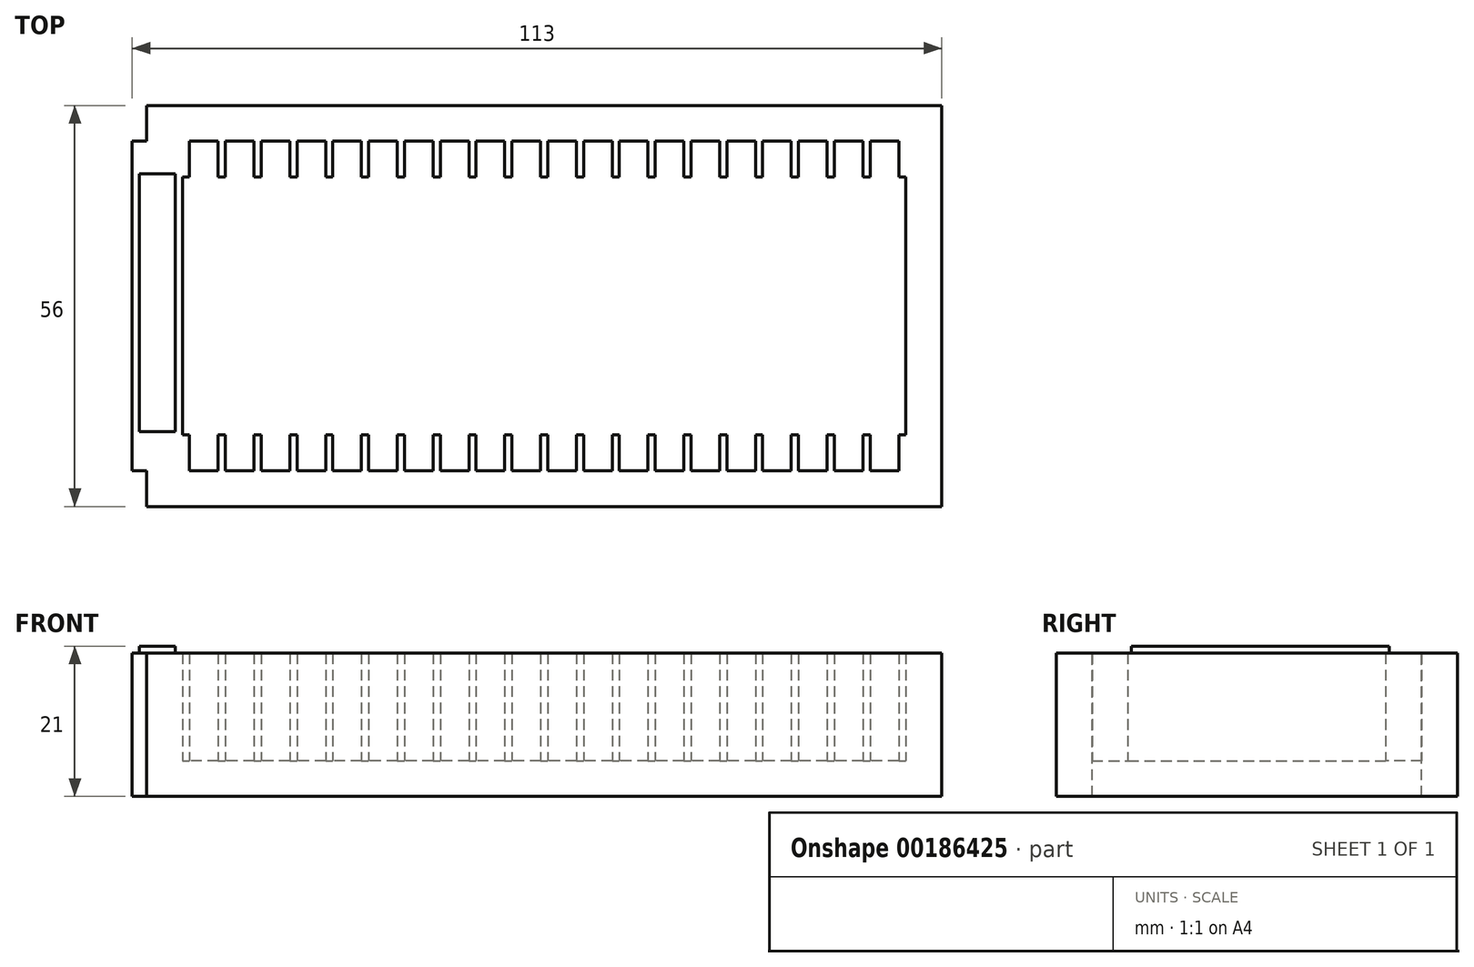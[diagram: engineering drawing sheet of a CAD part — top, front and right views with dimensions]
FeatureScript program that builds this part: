
annotation { "Feature Type Name" : "Feature", "Feature Type Description" : "" }
export const myFeature = defineFeature(function(context is Context, id is Id, definition is map)
    precondition{}
    {
        {
            var Q0;
            Q0=qCreatedBy(makeId("Top.planeOp"),FACE);
            var sketch = newSketch(context, id + "F0", { "sketchPlane" : qUnion([Q0])});
            skLineSegment(sketch, "E0.bottom", {"start": v(-50.5, 23) * mm, "end": v(50.5, 23) * mm});
            skLineSegment(sketch, "E0.top", {"start": v(-50.5, -23) * mm, "end": v(50.5, -23) * mm});
            skLineSegment(sketch, "E0.left", {"start": v(-50.5, 23) * mm, "end": v(-50.5, -23) * mm});
            skLineSegment(sketch, "E0.right", {"start": v(50.5, 23) * mm, "end": v(50.5, -23) * mm});
            skPoint(sketch, "E0.middle", {"position": v(0, 0) * mm});
            skSolve(sketch);
        }
        {
            var Q0;
            Q0=qCreatedBy(makeId("Top.planeOp"),FACE);
            var sketch = newSketch(context, id + "F1", { "sketchPlane" : qUnion([Q0])});
            skLineSegment(sketch, "E1.bottom", {"start": v(-50.5, 23) * mm, "end": v(-49.5, 23) * mm});
            skLineSegment(sketch, "E1.top", {"start": v(-50.5, 18) * mm, "end": v(-49.5, 18) * mm});
            skLineSegment(sketch, "E1.left", {"start": v(-50.5, 23) * mm, "end": v(-50.5, 18) * mm});
            skLineSegment(sketch, "E1.right", {"start": v(-49.5, 23) * mm, "end": v(-49.5, 18) * mm});
            skLineSegment(sketch, "E2.1.0.0", {"start": v(-45.5, 23) * mm, "end": v(-44.5, 23) * mm});
            skLineSegment(sketch, "E2.1.0.1", {"start": v(-45.5, 18) * mm, "end": v(-44.5, 18) * mm});
            skLineSegment(sketch, "E2.1.0.2", {"start": v(-45.5, 23) * mm, "end": v(-45.5, 18) * mm});
            skLineSegment(sketch, "E2.1.0.3", {"start": v(-44.5, 23) * mm, "end": v(-44.5, 18) * mm});
            skLineSegment(sketch, "E2.2.0.0", {"start": v(-40.5, 23) * mm, "end": v(-39.5, 23) * mm});
            skLineSegment(sketch, "E2.2.0.1", {"start": v(-40.5, 18) * mm, "end": v(-39.5, 18) * mm});
            skLineSegment(sketch, "E2.2.0.2", {"start": v(-40.5, 23) * mm, "end": v(-40.5, 18) * mm});
            skLineSegment(sketch, "E2.2.0.3", {"start": v(-39.5, 23) * mm, "end": v(-39.5, 18) * mm});
            skLineSegment(sketch, "E2.3.0.0", {"start": v(-35.5, 23) * mm, "end": v(-34.5, 23) * mm});
            skLineSegment(sketch, "E2.3.0.1", {"start": v(-35.5, 18) * mm, "end": v(-34.5, 18) * mm});
            skLineSegment(sketch, "E2.3.0.2", {"start": v(-35.5, 23) * mm, "end": v(-35.5, 18) * mm});
            skLineSegment(sketch, "E2.3.0.3", {"start": v(-34.5, 23) * mm, "end": v(-34.5, 18) * mm});
            skLineSegment(sketch, "E2.4.0.0", {"start": v(-30.5, 23) * mm, "end": v(-29.5, 23) * mm});
            skLineSegment(sketch, "E2.4.0.1", {"start": v(-30.5, 18) * mm, "end": v(-29.5, 18) * mm});
            skLineSegment(sketch, "E2.4.0.2", {"start": v(-30.5, 23) * mm, "end": v(-30.5, 18) * mm});
            skLineSegment(sketch, "E2.4.0.3", {"start": v(-29.5, 23) * mm, "end": v(-29.5, 18) * mm});
            skLineSegment(sketch, "E2.5.0.0", {"start": v(-25.5, 23) * mm, "end": v(-24.5, 23) * mm});
            skLineSegment(sketch, "E2.5.0.1", {"start": v(-25.5, 18) * mm, "end": v(-24.5, 18) * mm});
            skLineSegment(sketch, "E2.5.0.2", {"start": v(-25.5, 23) * mm, "end": v(-25.5, 18) * mm});
            skLineSegment(sketch, "E2.5.0.3", {"start": v(-24.5, 23) * mm, "end": v(-24.5, 18) * mm});
            skLineSegment(sketch, "E2.6.0.0", {"start": v(-20.5, 23) * mm, "end": v(-19.5, 23) * mm});
            skLineSegment(sketch, "E2.6.0.1", {"start": v(-20.5, 18) * mm, "end": v(-19.5, 18) * mm});
            skLineSegment(sketch, "E2.6.0.2", {"start": v(-20.5, 23) * mm, "end": v(-20.5, 18) * mm});
            skLineSegment(sketch, "E2.6.0.3", {"start": v(-19.5, 23) * mm, "end": v(-19.5, 18) * mm});
            skLineSegment(sketch, "E2.7.0.0", {"start": v(-15.5, 23) * mm, "end": v(-14.5, 23) * mm});
            skLineSegment(sketch, "E2.7.0.1", {"start": v(-15.5, 18) * mm, "end": v(-14.5, 18) * mm});
            skLineSegment(sketch, "E2.7.0.2", {"start": v(-15.5, 23) * mm, "end": v(-15.5, 18) * mm});
            skLineSegment(sketch, "E2.7.0.3", {"start": v(-14.5, 23) * mm, "end": v(-14.5, 18) * mm});
            skLineSegment(sketch, "E2.8.0.0", {"start": v(-10.5, 23) * mm, "end": v(-9.5, 23) * mm});
            skLineSegment(sketch, "E2.8.0.1", {"start": v(-10.5, 18) * mm, "end": v(-9.5, 18) * mm});
            skLineSegment(sketch, "E2.8.0.2", {"start": v(-10.5, 23) * mm, "end": v(-10.5, 18) * mm});
            skLineSegment(sketch, "E2.8.0.3", {"start": v(-9.5, 23) * mm, "end": v(-9.5, 18) * mm});
            skLineSegment(sketch, "E2.9.0.0", {"start": v(-5.5, 23) * mm, "end": v(-4.5, 23) * mm});
            skLineSegment(sketch, "E2.9.0.1", {"start": v(-5.5, 18) * mm, "end": v(-4.5, 18) * mm});
            skLineSegment(sketch, "E2.9.0.2", {"start": v(-5.5, 23) * mm, "end": v(-5.5, 18) * mm});
            skLineSegment(sketch, "E2.9.0.3", {"start": v(-4.5, 23) * mm, "end": v(-4.5, 18) * mm});
            skLineSegment(sketch, "E2.10.0.0", {"start": v(-0.5, 23) * mm, "end": v(0.5, 23) * mm});
            skLineSegment(sketch, "E2.10.0.1", {"start": v(-0.5, 18) * mm, "end": v(0.5, 18) * mm});
            skLineSegment(sketch, "E2.10.0.2", {"start": v(-0.5, 23) * mm, "end": v(-0.5, 18) * mm});
            skLineSegment(sketch, "E2.10.0.3", {"start": v(0.5, 23) * mm, "end": v(0.5, 18) * mm});
            skLineSegment(sketch, "E2.11.0.0", {"start": v(4.5, 23) * mm, "end": v(5.5, 23) * mm});
            skLineSegment(sketch, "E2.11.0.1", {"start": v(4.5, 18) * mm, "end": v(5.5, 18) * mm});
            skLineSegment(sketch, "E2.11.0.2", {"start": v(4.5, 23) * mm, "end": v(4.5, 18) * mm});
            skLineSegment(sketch, "E2.11.0.3", {"start": v(5.5, 23) * mm, "end": v(5.5, 18) * mm});
            skLineSegment(sketch, "E2.12.0.0", {"start": v(9.5, 23) * mm, "end": v(10.5, 23) * mm});
            skLineSegment(sketch, "E2.12.0.1", {"start": v(9.5, 18) * mm, "end": v(10.5, 18) * mm});
            skLineSegment(sketch, "E2.12.0.2", {"start": v(9.5, 23) * mm, "end": v(9.5, 18) * mm});
            skLineSegment(sketch, "E2.12.0.3", {"start": v(10.5, 23) * mm, "end": v(10.5, 18) * mm});
            skLineSegment(sketch, "E2.13.0.0", {"start": v(14.5, 23) * mm, "end": v(15.5, 23) * mm});
            skLineSegment(sketch, "E2.13.0.1", {"start": v(14.5, 18) * mm, "end": v(15.5, 18) * mm});
            skLineSegment(sketch, "E2.13.0.2", {"start": v(14.5, 23) * mm, "end": v(14.5, 18) * mm});
            skLineSegment(sketch, "E2.13.0.3", {"start": v(15.5, 23) * mm, "end": v(15.5, 18) * mm});
            skLineSegment(sketch, "E2.14.0.0", {"start": v(19.5, 23) * mm, "end": v(20.5, 23) * mm});
            skLineSegment(sketch, "E2.14.0.1", {"start": v(19.5, 18) * mm, "end": v(20.5, 18) * mm});
            skLineSegment(sketch, "E2.14.0.2", {"start": v(19.5, 23) * mm, "end": v(19.5, 18) * mm});
            skLineSegment(sketch, "E2.14.0.3", {"start": v(20.5, 23) * mm, "end": v(20.5, 18) * mm});
            skLineSegment(sketch, "E2.15.0.0", {"start": v(24.5, 23) * mm, "end": v(25.5, 23) * mm});
            skLineSegment(sketch, "E2.15.0.1", {"start": v(24.5, 18) * mm, "end": v(25.5, 18) * mm});
            skLineSegment(sketch, "E2.15.0.2", {"start": v(24.5, 23) * mm, "end": v(24.5, 18) * mm});
            skLineSegment(sketch, "E2.15.0.3", {"start": v(25.5, 23) * mm, "end": v(25.5, 18) * mm});
            skLineSegment(sketch, "E2.16.0.0", {"start": v(29.5, 23) * mm, "end": v(30.5, 23) * mm});
            skLineSegment(sketch, "E2.16.0.1", {"start": v(29.5, 18) * mm, "end": v(30.5, 18) * mm});
            skLineSegment(sketch, "E2.16.0.2", {"start": v(29.5, 23) * mm, "end": v(29.5, 18) * mm});
            skLineSegment(sketch, "E2.16.0.3", {"start": v(30.5, 23) * mm, "end": v(30.5, 18) * mm});
            skLineSegment(sketch, "E2.17.0.0", {"start": v(34.5, 23) * mm, "end": v(35.5, 23) * mm});
            skLineSegment(sketch, "E2.17.0.1", {"start": v(34.5, 18) * mm, "end": v(35.5, 18) * mm});
            skLineSegment(sketch, "E2.17.0.2", {"start": v(34.5, 23) * mm, "end": v(34.5, 18) * mm});
            skLineSegment(sketch, "E2.17.0.3", {"start": v(35.5, 23) * mm, "end": v(35.5, 18) * mm});
            skLineSegment(sketch, "E2.18.0.0", {"start": v(39.5, 23) * mm, "end": v(40.5, 23) * mm});
            skLineSegment(sketch, "E2.18.0.1", {"start": v(39.5, 18) * mm, "end": v(40.5, 18) * mm});
            skLineSegment(sketch, "E2.18.0.2", {"start": v(39.5, 23) * mm, "end": v(39.5, 18) * mm});
            skLineSegment(sketch, "E2.18.0.3", {"start": v(40.5, 23) * mm, "end": v(40.5, 18) * mm});
            skLineSegment(sketch, "E2.19.0.0", {"start": v(44.5, 23) * mm, "end": v(45.5, 23) * mm});
            skLineSegment(sketch, "E2.19.0.1", {"start": v(44.5, 18) * mm, "end": v(45.5, 18) * mm});
            skLineSegment(sketch, "E2.19.0.2", {"start": v(44.5, 23) * mm, "end": v(44.5, 18) * mm});
            skLineSegment(sketch, "E2.19.0.3", {"start": v(45.5, 23) * mm, "end": v(45.5, 18) * mm});
            skLineSegment(sketch, "E2.20.0.0", {"start": v(49.5, 23) * mm, "end": v(50.5, 23) * mm});
            skLineSegment(sketch, "E2.20.0.1", {"start": v(49.5, 18) * mm, "end": v(50.5, 18) * mm});
            skLineSegment(sketch, "E2.20.0.2", {"start": v(49.5, 23) * mm, "end": v(49.5, 18) * mm});
            skLineSegment(sketch, "E2.20.0.3", {"start": v(50.5, 23) * mm, "end": v(50.5, 18) * mm});
            skLineSegment(sketch, "E2.direction1", {"start": v(-50.5, 18) * mm, "end": v(-45.5, 18) * mm, "construction": true});
            skLineSegment(sketch, "E3.MirrorCS", {"start": v(-50.5, -23) * mm, "end": v(-49.5, -23) * mm});
            skLineSegment(sketch, "E4.MirrorCS", {"start": v(49.5, -23) * mm, "end": v(50.5, -23) * mm});
            skLineSegment(sketch, "E5.MirrorCS", {"start": v(-45.5, -18) * mm, "end": v(-44.5, -18) * mm});
            skLineSegment(sketch, "E6.MirrorCS", {"start": v(-50.5, -18) * mm, "end": v(-49.5, -18) * mm});
            skLineSegment(sketch, "E7.MirrorCS", {"start": v(-0.5, -18) * mm, "end": v(0.5, -18) * mm});
            skLineSegment(sketch, "E8.MirrorCS", {"start": v(19.5, -18) * mm, "end": v(20.5, -18) * mm});
            skLineSegment(sketch, "E9.MirrorCS", {"start": v(39.5, -18) * mm, "end": v(40.5, -18) * mm});
            skLineSegment(sketch, "E10.MirrorCS", {"start": v(-20.5, -18) * mm, "end": v(-19.5, -18) * mm});
            skLineSegment(sketch, "E11.MirrorCS", {"start": v(29.5, -18) * mm, "end": v(30.5, -18) * mm});
            skLineSegment(sketch, "E12.MirrorCS", {"start": v(49.5, -18) * mm, "end": v(50.5, -18) * mm});
            skLineSegment(sketch, "E13.MirrorCS", {"start": v(-35.5, -23) * mm, "end": v(-34.5, -23) * mm});
            skLineSegment(sketch, "E14.MirrorCS", {"start": v(-30.5, -18) * mm, "end": v(-29.5, -18) * mm});
            skLineSegment(sketch, "E15.MirrorCS", {"start": v(-10.5, -18) * mm, "end": v(-9.5, -18) * mm});
            skLineSegment(sketch, "E16.MirrorCS", {"start": v(9.5, -18) * mm, "end": v(10.5, -18) * mm});
            skLineSegment(sketch, "E17.MirrorCS", {"start": v(-40.5, -18) * mm, "end": v(-39.5, -18) * mm});
            skLineSegment(sketch, "E18.MirrorCS", {"start": v(-40.5, -23) * mm, "end": v(-39.5, -23) * mm});
            skLineSegment(sketch, "E19.MirrorCS", {"start": v(-0.5, -23) * mm, "end": v(0.5, -23) * mm});
            skLineSegment(sketch, "E20.MirrorCS", {"start": v(39.5, -23) * mm, "end": v(40.5, -23) * mm});
            skLineSegment(sketch, "E21.MirrorCS", {"start": v(19.5, -23) * mm, "end": v(20.5, -23) * mm});
            skLineSegment(sketch, "E22.MirrorCS", {"start": v(-45.5, -23) * mm, "end": v(-44.5, -23) * mm});
            skLineSegment(sketch, "E23.MirrorCS", {"start": v(-20.5, -23) * mm, "end": v(-19.5, -23) * mm});
            skLineSegment(sketch, "E24.MirrorCS", {"start": v(-35.5, -18) * mm, "end": v(-34.5, -18) * mm});
            skLineSegment(sketch, "E25.MirrorCS", {"start": v(-30.5, -23) * mm, "end": v(-29.5, -23) * mm});
            skLineSegment(sketch, "E26.MirrorCS", {"start": v(-10.5, -23) * mm, "end": v(-9.5, -23) * mm});
            skLineSegment(sketch, "E27.MirrorCS", {"start": v(9.5, -23) * mm, "end": v(10.5, -23) * mm});
            skLineSegment(sketch, "E28.MirrorCS", {"start": v(29.5, -23) * mm, "end": v(30.5, -23) * mm});
            skLineSegment(sketch, "E29.MirrorCS", {"start": v(34.5, -18) * mm, "end": v(35.5, -18) * mm});
            skLineSegment(sketch, "E30.MirrorCS", {"start": v(-25.5, -18) * mm, "end": v(-24.5, -18) * mm});
            skLineSegment(sketch, "E31.MirrorCS", {"start": v(-5.5, -18) * mm, "end": v(-4.5, -18) * mm});
            skLineSegment(sketch, "E32.MirrorCS", {"start": v(14.5, -18) * mm, "end": v(15.5, -18) * mm});
            skLineSegment(sketch, "E33.MirrorCS", {"start": v(4.5, -23) * mm, "end": v(5.5, -23) * mm});
            skLineSegment(sketch, "E34.MirrorCS", {"start": v(24.5, -23) * mm, "end": v(25.5, -23) * mm});
            skLineSegment(sketch, "E35.MirrorCS", {"start": v(44.5, -23) * mm, "end": v(45.5, -23) * mm});
            skLineSegment(sketch, "E36.MirrorCS", {"start": v(-15.5, -23) * mm, "end": v(-14.5, -23) * mm});
            skLineSegment(sketch, "E37.MirrorCS", {"start": v(24.5, -18) * mm, "end": v(25.5, -18) * mm});
            skLineSegment(sketch, "E38.MirrorCS", {"start": v(34.5, -23) * mm, "end": v(35.5, -23) * mm});
            skLineSegment(sketch, "E39.MirrorCS", {"start": v(44.5, -18) * mm, "end": v(45.5, -18) * mm});
            skLineSegment(sketch, "E40.MirrorCS", {"start": v(-25.5, -23) * mm, "end": v(-24.5, -23) * mm});
            skLineSegment(sketch, "E41.MirrorCS", {"start": v(-15.5, -18) * mm, "end": v(-14.5, -18) * mm});
            skLineSegment(sketch, "E42.MirrorCS", {"start": v(-5.5, -23) * mm, "end": v(-4.5, -23) * mm});
            skLineSegment(sketch, "E43.MirrorCS", {"start": v(14.5, -23) * mm, "end": v(15.5, -23) * mm});
            skLineSegment(sketch, "E44.MirrorCS", {"start": v(4.5, -18) * mm, "end": v(5.5, -18) * mm});
            skLineSegment(sketch, "E45.MirrorCS", {"start": v(-49.5, -23) * mm, "end": v(-49.5, -18) * mm});
            skLineSegment(sketch, "E46.MirrorCS", {"start": v(-50.5, -23) * mm, "end": v(-50.5, -18) * mm});
            skLineSegment(sketch, "E47.MirrorCS", {"start": v(30.5, -23) * mm, "end": v(30.5, -18) * mm});
            skLineSegment(sketch, "E48.MirrorCS", {"start": v(50.5, -23) * mm, "end": v(50.5, -18) * mm});
            skLineSegment(sketch, "E49.MirrorCS", {"start": v(-29.5, -23) * mm, "end": v(-29.5, -18) * mm});
            skLineSegment(sketch, "E50.MirrorCS", {"start": v(-9.5, -23) * mm, "end": v(-9.5, -18) * mm});
            skLineSegment(sketch, "E51.MirrorCS", {"start": v(10.5, -23) * mm, "end": v(10.5, -18) * mm});
            skLineSegment(sketch, "E52.MirrorCS", {"start": v(-0.5, -23) * mm, "end": v(-0.5, -18) * mm});
            skLineSegment(sketch, "E53.MirrorCS", {"start": v(19.5, -23) * mm, "end": v(19.5, -18) * mm});
            skLineSegment(sketch, "E54.MirrorCS", {"start": v(39.5, -23) * mm, "end": v(39.5, -18) * mm});
            skLineSegment(sketch, "E55.MirrorCS", {"start": v(-20.5, -23) * mm, "end": v(-20.5, -18) * mm});
            skLineSegment(sketch, "E56.MirrorCS", {"start": v(29.5, -23) * mm, "end": v(29.5, -18) * mm});
            skLineSegment(sketch, "E57.MirrorCS", {"start": v(49.5, -23) * mm, "end": v(49.5, -18) * mm});
            skLineSegment(sketch, "E58.MirrorCS", {"start": v(-10.5, -23) * mm, "end": v(-10.5, -18) * mm});
            skLineSegment(sketch, "E59.MirrorCS", {"start": v(-30.5, -23) * mm, "end": v(-30.5, -18) * mm});
            skLineSegment(sketch, "E60.MirrorCS", {"start": v(9.5, -23) * mm, "end": v(9.5, -18) * mm});
            skLineSegment(sketch, "E61.MirrorCS", {"start": v(-39.5, -23) * mm, "end": v(-39.5, -18) * mm});
            skLineSegment(sketch, "E62.MirrorCS", {"start": v(-40.5, -23) * mm, "end": v(-40.5, -18) * mm});
            skLineSegment(sketch, "E63.MirrorCS", {"start": v(-44.5, -23) * mm, "end": v(-44.5, -18) * mm});
            skLineSegment(sketch, "E64.MirrorCS", {"start": v(-45.5, -23) * mm, "end": v(-45.5, -18) * mm});
            skLineSegment(sketch, "E65.MirrorCS", {"start": v(-34.5, -23) * mm, "end": v(-34.5, -18) * mm});
            skLineSegment(sketch, "E66.MirrorCS", {"start": v(-35.5, -23) * mm, "end": v(-35.5, -18) * mm});
            skLineSegment(sketch, "E67.MirrorCS", {"start": v(-4.5, -23) * mm, "end": v(-4.5, -18) * mm});
            skLineSegment(sketch, "E68.MirrorCS", {"start": v(15.5, -23) * mm, "end": v(15.5, -18) * mm});
            skLineSegment(sketch, "E69.MirrorCS", {"start": v(35.5, -23) * mm, "end": v(35.5, -18) * mm});
            skLineSegment(sketch, "E70.MirrorCS", {"start": v(-24.5, -23) * mm, "end": v(-24.5, -18) * mm});
            skLineSegment(sketch, "E71.MirrorCS", {"start": v(25.5, -23) * mm, "end": v(25.5, -18) * mm});
            skLineSegment(sketch, "E72.MirrorCS", {"start": v(45.5, -23) * mm, "end": v(45.5, -18) * mm});
            skLineSegment(sketch, "E73.MirrorCS", {"start": v(34.5, -23) * mm, "end": v(34.5, -18) * mm});
            skLineSegment(sketch, "E74.MirrorCS", {"start": v(-25.5, -23) * mm, "end": v(-25.5, -18) * mm});
            skLineSegment(sketch, "E75.MirrorCS", {"start": v(-5.5, -23) * mm, "end": v(-5.5, -18) * mm});
            skLineSegment(sketch, "E76.MirrorCS", {"start": v(-14.5, -23) * mm, "end": v(-14.5, -18) * mm});
            skLineSegment(sketch, "E77.MirrorCS", {"start": v(14.5, -23) * mm, "end": v(14.5, -18) * mm});
            skLineSegment(sketch, "E78.MirrorCS", {"start": v(5.5, -23) * mm, "end": v(5.5, -18) * mm});
            skLineSegment(sketch, "E79.MirrorCS", {"start": v(24.5, -23) * mm, "end": v(24.5, -18) * mm});
            skLineSegment(sketch, "E80.MirrorCS", {"start": v(44.5, -23) * mm, "end": v(44.5, -18) * mm});
            skLineSegment(sketch, "E81.MirrorCS", {"start": v(-15.5, -23) * mm, "end": v(-15.5, -18) * mm});
            skLineSegment(sketch, "E82.MirrorCS", {"start": v(4.5, -23) * mm, "end": v(4.5, -18) * mm});
            skLineSegment(sketch, "E83.MirrorCS", {"start": v(-50.5, -18) * mm, "end": v(-45.5, -18) * mm, "construction": true});
            skLineSegment(sketch, "E84.MirrorCS", {"start": v(0.5, -23) * mm, "end": v(0.5, -18) * mm});
            skLineSegment(sketch, "E85.MirrorCS", {"start": v(20.5, -23) * mm, "end": v(20.5, -18) * mm});
            skLineSegment(sketch, "E86.MirrorCS", {"start": v(40.5, -23) * mm, "end": v(40.5, -18) * mm});
            skLineSegment(sketch, "E87.MirrorCS", {"start": v(-19.5, -23) * mm, "end": v(-19.5, -18) * mm});
            skSolve(sketch);
        }
        {
            var Q0;
            Q0=qCreatedBy(makeId("Front.planeOp"),FACE);
            var sketch = newSketch(context, id + "F2", { "sketchPlane" : qUnion([Q0])});
            skLineSegment(sketch, "E88.bottom", {"start": v(50.5, 2.5) * mm, "end": v(-50.5, 2.5) * mm});
            skLineSegment(sketch, "E88.top", {"start": v(50.5, -2.5) * mm, "end": v(-50.5, -2.5) * mm});
            skLineSegment(sketch, "E88.left", {"start": v(50.5, 2.5) * mm, "end": v(50.5, -2.5) * mm});
            skLineSegment(sketch, "E88.right", {"start": v(-50.5, 2.5) * mm, "end": v(-50.5, -2.5) * mm});
            skPoint(sketch, "E88.middle", {"position": v(0, 0) * mm});
            skLineSegment(sketch, "E89.bottom", {"start": v(-50.5, -2.5) * mm, "end": v(-57.5, -2.5) * mm});
            skLineSegment(sketch, "E89.top", {"start": v(-50.5, 17.5) * mm, "end": v(-57.5, 17.5) * mm});
            skLineSegment(sketch, "E89.left", {"start": v(-50.5, -2.5) * mm, "end": v(-50.5, 17.5) * mm});
            skLineSegment(sketch, "E89.right", {"start": v(-57.5, -2.5) * mm, "end": v(-57.5, 17.5) * mm});
            skLineSegment(sketch, "E90.bottom", {"start": v(50.5, -2.5) * mm, "end": v(55.5, -2.5) * mm});
            skLineSegment(sketch, "E90.top", {"start": v(50.5, 17.5) * mm, "end": v(55.5, 17.5) * mm});
            skLineSegment(sketch, "E90.left", {"start": v(50.5, -2.5) * mm, "end": v(50.5, 17.5) * mm});
            skLineSegment(sketch, "E90.right", {"start": v(55.5, -2.5) * mm, "end": v(55.5, 17.5) * mm});
            skSolve(sketch);
        }
        {
            var Q0;
            Q0 = qSketchRegion(id + "F2", true);
            extrude(context, id + "F3", {"entities" : qUnion([Q0]), "endBound" : BoundingType.SYMMETRIC, "depth" : 46 * mm});
        }
        {
            var Q0;
            Q0=qCreatedBy(makeId("Right.planeOp"),FACE);
            var sketch = newSketch(context, id + "F4", { "sketchPlane" : qUnion([Q0])});
            skLineSegment(sketch, "E91.bottom", {"start": v(-23, 17.5) * mm, "end": v(-28, 17.5) * mm});
            skLineSegment(sketch, "E91.top", {"start": v(-23, -2.5) * mm, "end": v(-28, -2.5) * mm});
            skLineSegment(sketch, "E91.left", {"start": v(-23, 17.5) * mm, "end": v(-23, -2.5) * mm});
            skLineSegment(sketch, "E91.right", {"start": v(-28, 17.5) * mm, "end": v(-28, -2.5) * mm});
            skLineSegment(sketch, "E92.MirrorCS", {"start": v(28, 17.5) * mm, "end": v(28, -2.5) * mm});
            skLineSegment(sketch, "E93.MirrorCS", {"start": v(23, 17.5) * mm, "end": v(23, -2.5) * mm});
            skLineSegment(sketch, "E94.MirrorCS", {"start": v(23, -2.5) * mm, "end": v(28, -2.5) * mm});
            skLineSegment(sketch, "E95.MirrorCS", {"start": v(23, 17.5) * mm, "end": v(28, 17.5) * mm});
            skSolve(sketch);
        }
        {
            var Q0;
            Q0 = qSketchRegion(id + "F4", true);
            extrude(context, id + "F5", {"entities" : qUnion([Q0]), "operationType" : NewBodyOperationType.ADD, "endBound" : BoundingType.SYMMETRIC, "depth" : 111 * mm});
        }
        {
            var Q0;
            Q0 = qSketchRegion(id + "F1", true);
            extrude(context, id + "F6", {"entities" : qUnion([Q0]), "operationType" : NewBodyOperationType.ADD, "depth" : 17.5 * mm});
        }
        {
            var Q0;
            Q0=qCreatedBy(makeId("Top.planeOp"),FACE);
            var sketch = newSketch(context, id + "F7", { "sketchPlane" : qUnion([Q0])});
            skLineSegment(sketch, "E96.bottom", {"start": v(-56.5, 18.47) * mm, "end": v(-51.5, 18.47) * mm});
            skLineSegment(sketch, "E96.top", {"start": v(-56.5, -17.53) * mm, "end": v(-51.5, -17.53) * mm});
            skLineSegment(sketch, "E96.left", {"start": v(-56.5, 18.47) * mm, "end": v(-56.5, -17.53) * mm});
            skLineSegment(sketch, "E96.right", {"start": v(-51.5, 18.47) * mm, "end": v(-51.5, -17.53) * mm});
            skSolve(sketch);
        }
        {
            var Q0;
            Q0 = qSketchRegion(id + "F7", true);
            extrude(context, id + "F8", {"entities" : qUnion([Q0]), "operationType" : NewBodyOperationType.ADD, "depth" : 18.5 * mm});
        }
    });
